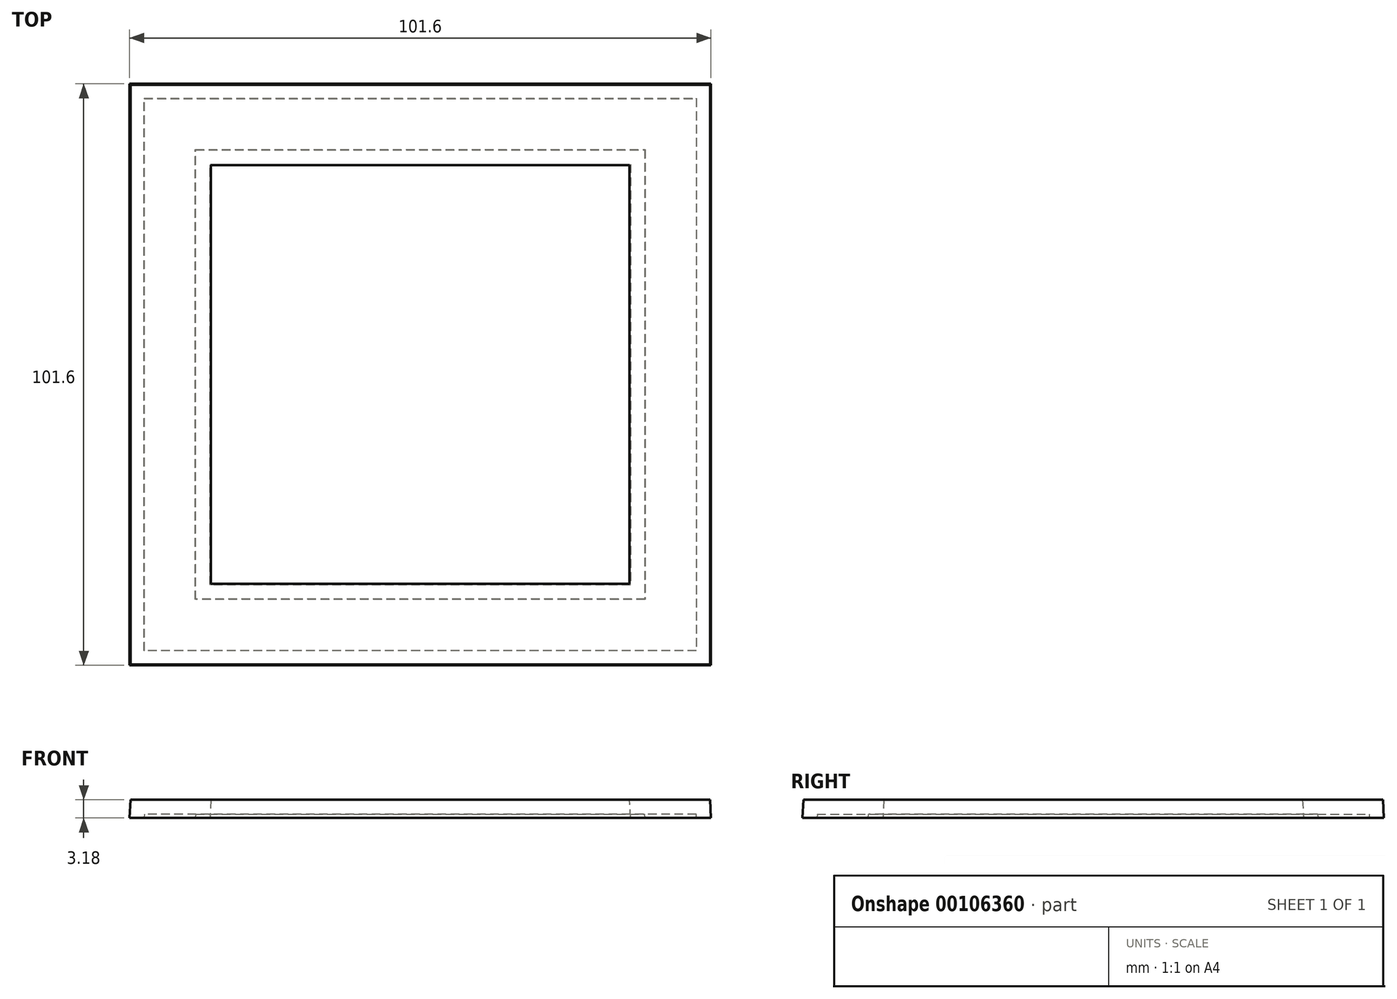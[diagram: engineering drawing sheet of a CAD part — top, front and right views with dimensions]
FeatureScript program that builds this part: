
annotation { "Feature Type Name" : "Feature", "Feature Type Description" : "" }
export const myFeature = defineFeature(function(context is Context, id is Id, definition is map)
    precondition{}
    {
        {
            var Q0;
            Q0=qCreatedBy(makeId("Top.planeOp"),FACE);
            var sketch = newSketch(context, id + "F0", { "sketchPlane" : qUnion([Q0])});
            skLineSegment(sketch, "E0.bottom", {"start": v(50.8, -50.8) * mm, "end": v(-50.8, -50.8) * mm});
            skLineSegment(sketch, "E0.top", {"start": v(50.8, 50.8) * mm, "end": v(-50.8, 50.8) * mm});
            skLineSegment(sketch, "E0.left", {"start": v(50.8, -50.8) * mm, "end": v(50.8, 50.8) * mm});
            skLineSegment(sketch, "E0.right", {"start": v(-50.8, -50.8) * mm, "end": v(-50.8, 50.8) * mm});
            skPoint(sketch, "E0.middle", {"position": v(0, 0) * mm});
            skSolve(sketch);
        }
        {
            var Q0;
            Q0=qSketchRegion(id+"F0",true);
            extrude(context, id + "F1", {"entities" : qUnion([Q0]), "depth" : 3.17 * mm, "hasDraft" : true, "draftAngle" : 3 * degree, "draftPullDirection" : true});
        }
        {
            var Q0;
            Q0=makeQuery(id+"F1.opExtrude","CAP_FACE",FACE,{"disambiguationData":[OSD([sQuery(id+"F0.wireOp",EDGE,"E0.bottom"),sQuery(id+"F0.wireOp",EDGE,"E0.top"),sQuery(id+"F0.wireOp",EDGE,"E0.left"),sQuery(id+"F0.wireOp",EDGE,"E0.right")])],"isStart":false});
            var Q1;
            Q1=makeQuery(id+"F1.opExtrude","CAP_FACE",FACE,{"disambiguationData":[OSD([sQuery(id+"F0.wireOp",EDGE,"E0.bottom"),sQuery(id+"F0.wireOp",EDGE,"E0.top"),sQuery(id+"F0.wireOp",EDGE,"E0.left"),sQuery(id+"F0.wireOp",EDGE,"E0.right")])],"isStart":true});
            shell(context, id + "F2", {"entities" : qUnion([Q0, Q1]), "thickness" : 14.03 * mm});
        }
        {
            var Q0;
            Q0=qCreatedBy(makeId("Front.planeOp"),FACE);
            var sketch = newSketch(context, id + "F3", { "sketchPlane" : qUnion([Q0])});
            skLineSegment(sketch, "E1", {"start": v(0, 0) * mm, "end": v(0, 138.81) * mm});
            skSolve(sketch);
        }
        {
            var Q0;
            Q0=makeQuery(id+"F1.opExtrude","SWEPT_BODY",BODY,{"disambiguationData":[OSD([sQuery(id+"F0.wireOp",EDGE,"E0.bottom"),sQuery(id+"F0.wireOp",EDGE,"E0.top"),sQuery(id+"F0.wireOp",EDGE,"E0.left"),sQuery(id+"F0.wireOp",EDGE,"E0.right")])]});
            var Q1;
            Q1=sQuery(id+"F3.wireOp",EDGE,"E1");
            transform(context, id + "F4", {"entities" : qUnion([Q0]), "transformType" : TransformType.ROTATION, "transformAxis" : qUnion([Q1]), "angle" : 45 * degree, "makeCopy" : false});
        }
        {
            var Q0;
            Q0=makeQuery(id+"F1.opExtrude","SWEPT_BODY",BODY,{"disambiguationData":[OSD([sQuery(id+"F0.wireOp",EDGE,"E0.bottom"),sQuery(id+"F0.wireOp",EDGE,"E0.top"),sQuery(id+"F0.wireOp",EDGE,"E0.left"),sQuery(id+"F0.wireOp",EDGE,"E0.right")])]});
            var Q1;
            Q1=sQuery(id+"F3.wireOp",EDGE,"E1");
            transform(context, id + "F5", {"entities" : qUnion([Q0]), "transformType" : TransformType.ROTATION, "transformAxis" : qUnion([Q1]), "angle" : 315 * degree, "makeCopy" : false});
        }
        {
            var Q0;
            Q0=makeQuery(id+"F1.opExtrude","CAP_FACE",FACE,{"disambiguationData":[OSD([sQuery(id+"F0.wireOp",EDGE,"E0.bottom"),sQuery(id+"F0.wireOp",EDGE,"E0.top"),sQuery(id+"F0.wireOp",EDGE,"E0.left"),sQuery(id+"F0.wireOp",EDGE,"E0.right")])],"isStart":true});
            shell(context, id + "F6", {"entities" : qUnion([Q0]), "thickness" : 2.54 * mm});
        }
    });
